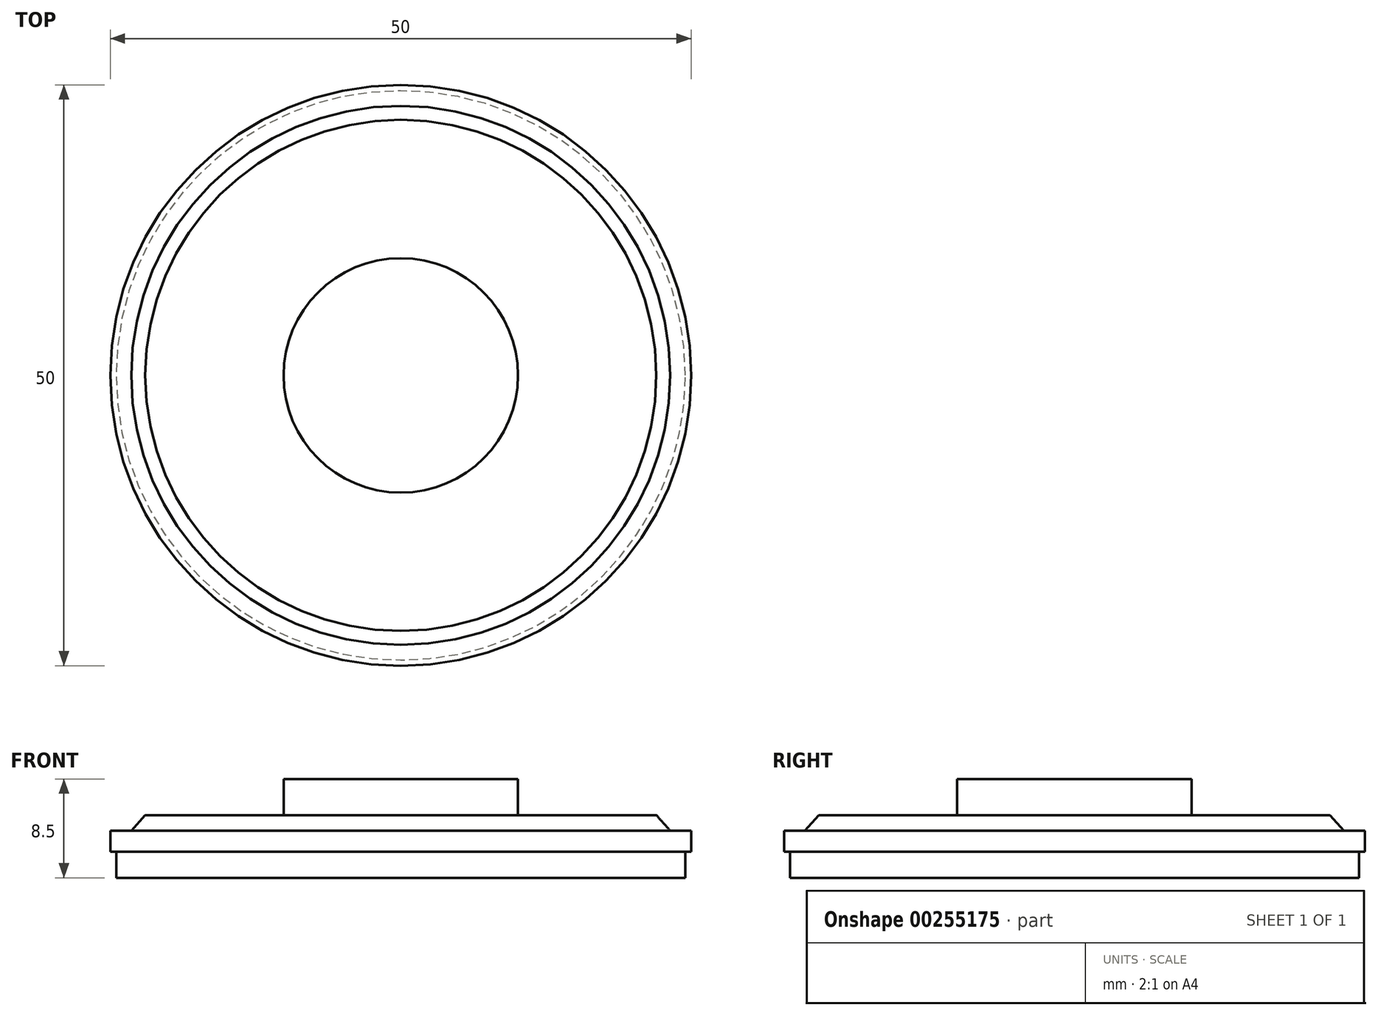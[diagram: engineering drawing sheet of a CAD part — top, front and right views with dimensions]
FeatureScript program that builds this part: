
annotation { "Feature Type Name" : "Feature", "Feature Type Description" : "" }
export const myFeature = defineFeature(function(context is Context, id is Id, definition is map)
    precondition{}
    {
        {
            var Q0;
            Q0=qCreatedBy(makeId("Front.planeOp"),FACE);
            var sketch = newSketch(context, id + "F0", { "sketchPlane" : qUnion([Q0])});
            skLineSegment(sketch, "E0", {"start": v(-24.5, 0) * mm, "end": v(-24.5, 2.25) * mm});
            skLineSegment(sketch, "E1", {"start": v(-24.5, 2.25) * mm, "end": v(-25, 2.25) * mm});
            skLineSegment(sketch, "E2", {"start": v(-25, 2.25) * mm, "end": v(-25, 4.05) * mm});
            skLineSegment(sketch, "E3", {"start": v(-25, 4.05) * mm, "end": v(-23.2, 4.05) * mm});
            skLineSegment(sketch, "E4", {"start": v(-23.2, 4.05) * mm, "end": v(-22, 5.4) * mm});
            skLineSegment(sketch, "E5", {"start": v(-22, 5.4) * mm, "end": v(-10.1, 5.4) * mm});
            skLineSegment(sketch, "E6", {"start": v(-10.1, 5.4) * mm, "end": v(-10.1, 8.5) * mm});
            skLineSegment(sketch, "E7", {"start": v(-10.1, 8.5) * mm, "end": v(0, 8.5) * mm});
            skLineSegment(sketch, "E8", {"start": v(0, 8.5) * mm, "end": v(0, 0) * mm});
            skLineSegment(sketch, "E9", {"start": v(0, 0) * mm, "end": v(-24.5, 0) * mm});
            skSolve(sketch);
        }
        {
            var Q0;
            Q0 = qSketchRegion(id + "F0", true);
            var Q1;
            Q1=sQuery(id+"F0.wireOp",EDGE,"E8");
            revolve(context, id + "F1", {"entities" : qUnion([Q0]), "axis" : qUnion([Q1]), "revolveType" : RevolveType.FULL});
        }
    });
